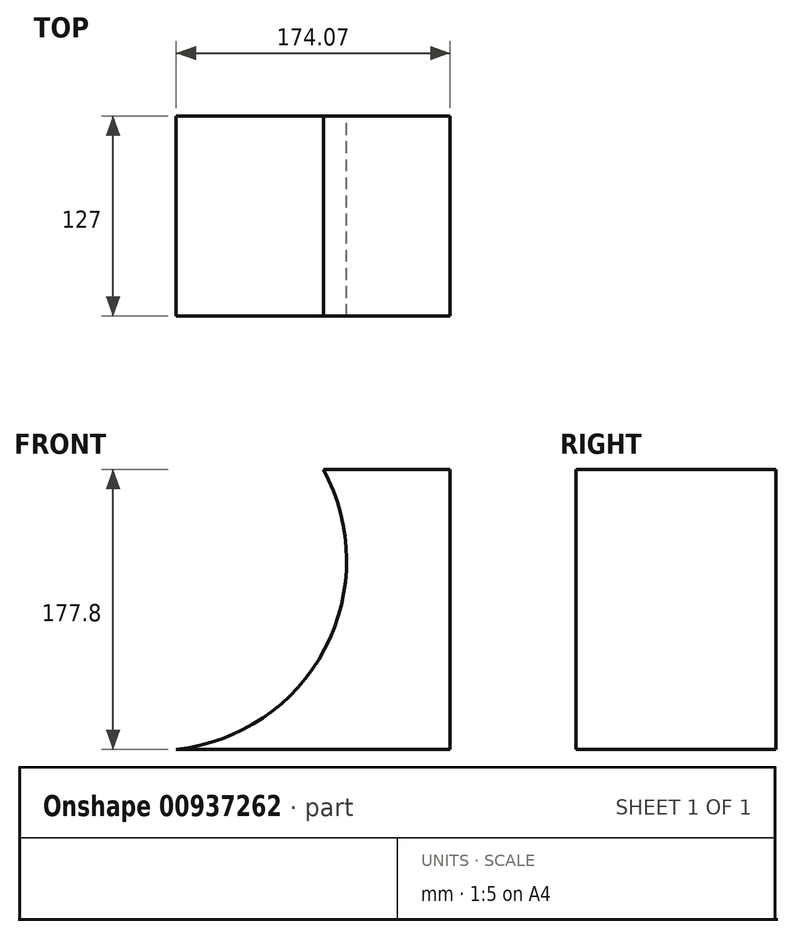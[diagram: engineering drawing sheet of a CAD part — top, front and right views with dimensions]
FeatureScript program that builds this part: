
annotation { "Feature Type Name" : "Feature", "Feature Type Description" : "" }
export const myFeature = defineFeature(function(context is Context, id is Id, definition is map)
    precondition{}
    {
        {
            var Q0;
            Q0=qCreatedBy(makeId("Front.planeOp"),FACE);
            var sketch = newSketch(context, id + "F0", { "sketchPlane" : qUnion([Q0])});
            skArc(sketch, "E0", {"start": v(-119.74, -100.9) * mm, "mid": v(-6.93, -47.71) * mm, "end": v(-1.52, 76.9) * mm});
            skLineSegment(sketch, "E1", {"start": v(-1.52, 76.9) * mm, "end": v(79.06, 76.9) * mm});
            skLineSegment(sketch, "E2", {"start": v(79.06, 76.9) * mm, "end": v(79.06, -100.9) * mm});
            skLineSegment(sketch, "E3", {"start": v(79.06, -100.9) * mm, "end": v(-119.74, -100.9) * mm});
            skSolve(sketch);
        }
        {
            var Q0;
            {var subQ0=sQuery(id+"F0.wireOp",EDGE,"E1");Q0=makeQuery(id+"F0.imprint","IMPRINT",FACE,{"disambiguationData":[TD([[makeQuery(id+"F0.imprint","IMPRINT",EDGE,{"derivedFrom":subQ0}),-1.0]])]});}
            extrude(context, id + "F1", {"entities" : qUnion([Q0]), "surfaceOperationType" : NewSurfaceOperationType.ADD, "depth" : 127 * mm, "offsetDistance" : 25.4 * mm});
        }
    });
